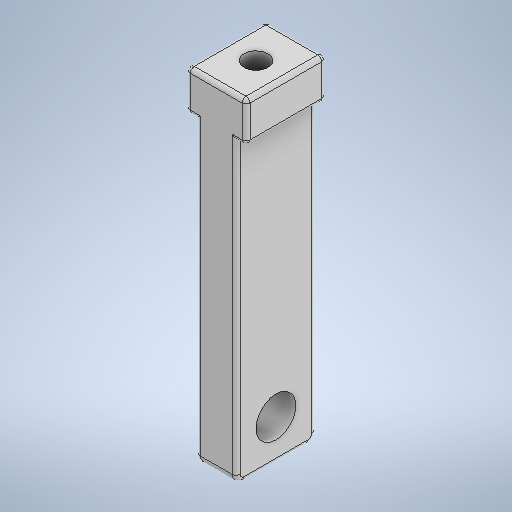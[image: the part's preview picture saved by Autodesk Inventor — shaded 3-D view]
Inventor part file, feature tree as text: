
AUTODESK INVENTOR PART (.ipt)
format: ipt  version: 2025.3 (Build 293356000, 356)  size: 298,496 bytes
history: native  units: mm
features: sketch x4, extrude x3, fillet x3, hole x1
ambient origin geometry x8: Origin, YZ Plane, XZ Plane, XY Plane, X Axis, Y Axis, Z Axis, Center Point
bodies: Solid1 (feature_tree)
feature tree (11):
  extrude  "Extrusion1"  Depth=85.0mm
  hole  "Hole1"  [1 undecoded]
  fillet  "Fillet1"  Radius=10.0mm
  extrude  "Extrusion3"  Depth=1.0mm
  extrude  "Extrusion2"  Depth=20.0mm TaperAngle=0.0deg
  fillet  "Fillet2"  Radius=15.0mm
  fillet  "Fillet3"  Radius=10.0mm
  sketch  "Sketch1"  dims[d0=10.0mm d1=85.0mm]
  sketch  "Sketch2"  dims[d2=20.0mm d3=0.0mm]
  sketch  "Sketch3"  dims[d6=10.0mm d7=6.0mm d8=4.0mm d9=2.0mm d10=90.0deg d11=8.0mm d12=20.594885mm d14=10.0mm d15=10.0mm]
  sketch  "Sketch4"  dims[d16=2.0mm d24=6.0mm d25=20.0mm d26=0.0mm d27=15.0mm d28=10.0mm d29=7.5mm d30=20.0mm d31=0.0mm d32=0.0mm d33=1.0mm d34=18.0mm d35=0.0mm d36=1.0mm]
note: 1 required parameter value undecoded (feature->parameter linkage not recoverable at this tier; creation-order binding heuristic only, values carry confidence <= 0.55)
